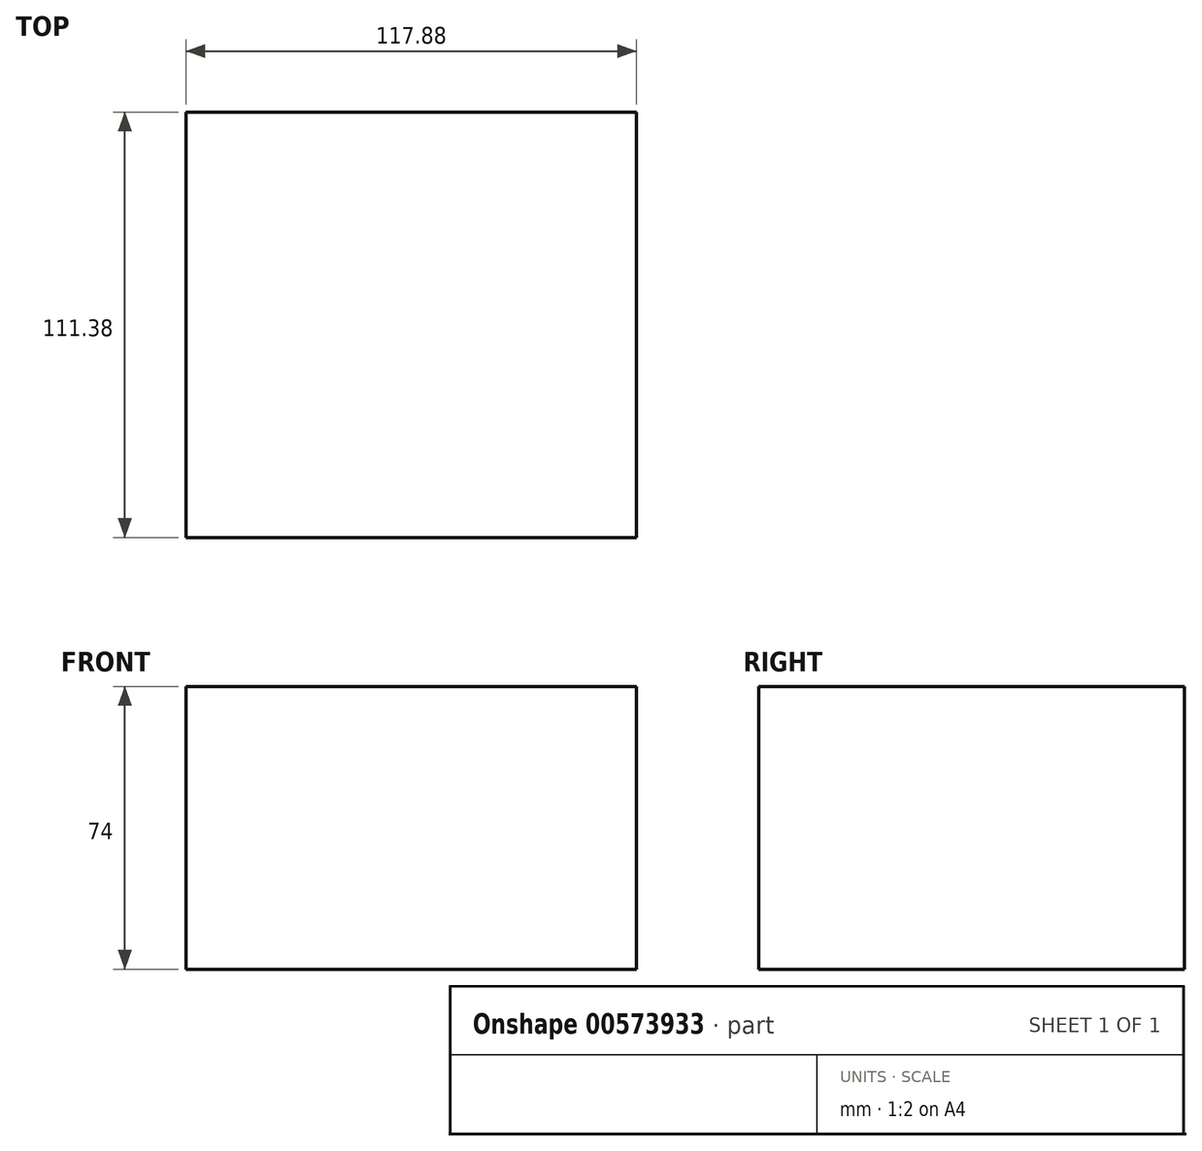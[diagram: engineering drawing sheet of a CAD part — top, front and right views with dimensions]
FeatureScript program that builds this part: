
annotation { "Feature Type Name" : "Feature", "Feature Type Description" : "" }
export const myFeature = defineFeature(function(context is Context, id is Id, definition is map)
    precondition{}
    {
        {
            var Q0;
            Q0=qCreatedBy(makeId("Top.planeOp"),FACE);
            var sketch = newSketch(context, id + "F0", { "sketchPlane" : qUnion([Q0])});
            skLineSegment(sketch, "E0.bottom", {"start": v(-58.06, -52.86) * mm, "end": v(59.82, -52.86) * mm});
            skLineSegment(sketch, "E0.top", {"start": v(-58.06, 58.52) * mm, "end": v(59.82, 58.52) * mm});
            skLineSegment(sketch, "E0.left", {"start": v(-58.06, -52.86) * mm, "end": v(-58.06, 58.52) * mm});
            skLineSegment(sketch, "E0.right", {"start": v(59.82, -52.86) * mm, "end": v(59.82, 58.52) * mm});
            skSolve(sketch);
        }
        {
            var Q0;
            Q0=makeQuery(id+"F0.imprint","IMPRINT",FACE,{"disambiguationData":[TD([[makeQuery(id+"F0.imprint","IMPRINT",EDGE,{"derivedFrom":sQuery(id+"F0.wireOp",EDGE,"E0.bottom")}),1.0]])]});
            extrude(context, id + "F1", {"entities" : qUnion([Q0]), "depth" : 74 * mm, "offsetDistance" : 25 * mm});
        }
    });
